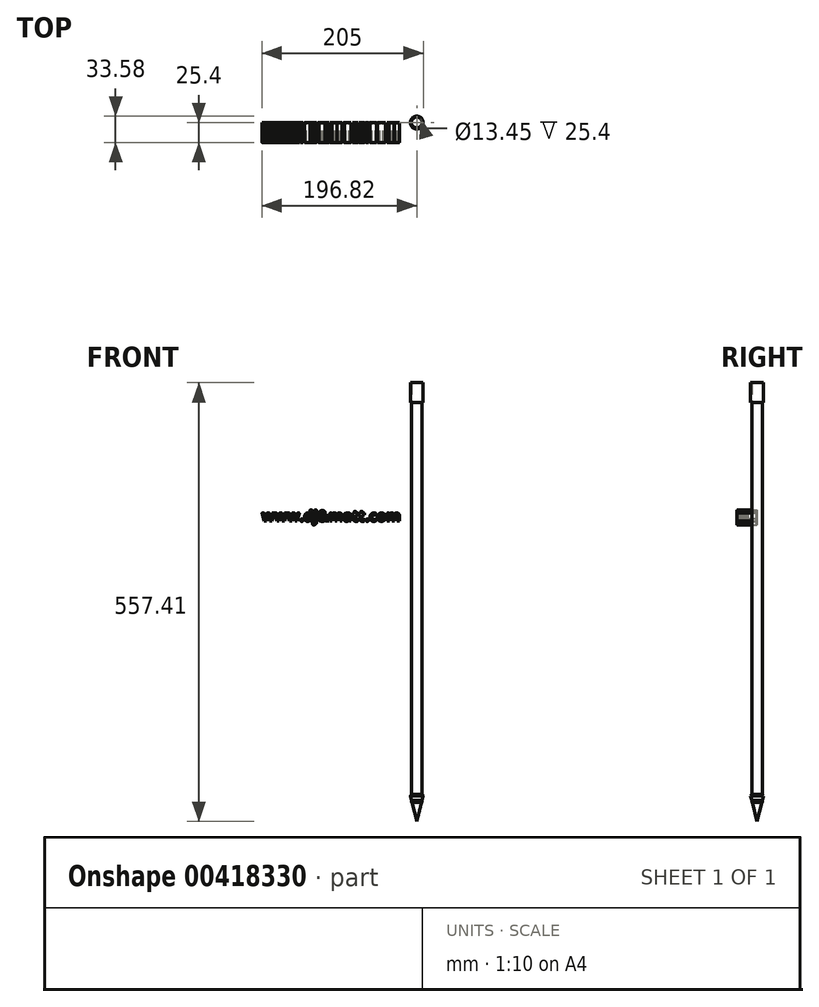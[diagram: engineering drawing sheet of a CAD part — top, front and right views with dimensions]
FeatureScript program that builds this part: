
annotation { "Feature Type Name" : "Feature", "Feature Type Description" : "" }
export const myFeature = defineFeature(function(context is Context, id is Id, definition is map)
    precondition{}
    {
        {
            var Q0;
            Q0=qCreatedBy(makeId("Top.planeOp"),FACE);
            var sketch = newSketch(context, id + "F0", { "sketchPlane" : qUnion([Q0])});
            skCircle(sketch, "E0", {"center": v(0, 0) * mm, "radius": 6.72 * mm});
            skSolve(sketch);
        }
        {
            var Q0;
            Q0=makeQuery(id+"F0.imprint","IMPRINT",FACE,{"disambiguationData":[TD([[makeQuery(id+"F0.imprint","IMPRINT",EDGE,{"derivedFrom":sQuery(id+"F0.wireOp",EDGE,"E0")}),1.0]])]});
            extrude(context, id + "F1", {"entities" : qUnion([Q0]), "depth" : 508 * mm});
        }
        {
            var Q0;
            Q0=qCreatedBy(makeId("Right.planeOp"),FACE);
            var sketch = newSketch(context, id + "F2", { "sketchPlane" : qUnion([Q0])});
            skLineSegment(sketch, "E1", {"start": v(0, -24.01) * mm, "end": v(8.18, 8.7) * mm});
            skLineSegment(sketch, "E2", {"start": v(8.18, 8.7) * mm, "end": v(0, 18.25) * mm});
            skLineSegment(sketch, "E3", {"start": v(0, 18.25) * mm, "end": v(0, -24.01) * mm});
            skSolve(sketch);
        }
        {
            var Q0;
            Q0=makeQuery(id+"F2.imprint","IMPRINT",FACE,{"disambiguationData":[TD([[makeQuery(id+"F2.imprint","IMPRINT",EDGE,{"derivedFrom":sQuery(id+"F2.wireOp",EDGE,"E1")}),1.0]])]});
            var Q1;
            Q1=sQuery(id+"F2.wireOp",EDGE,"E3");
            revolve(context, id + "F3", {"operationType" : NewBodyOperationType.ADD, "entities" : qUnion([Q0]), "axis" : qUnion([Q1]), "revolveType" : RevolveType.FULL});
        }
        {
            var Q0;
            Q0=makeQuery(id+"F1.opExtrude","CAP_FACE",FACE,{"disambiguationData":[OSD([sQuery(id+"F0.wireOp",EDGE,"E0")])],"isStart":false});
            var sketch = newSketch(context, id + "F4", { "sketchPlane" : qUnion([Q0])});
            skCircle(sketch, "E4", {"center": v(0, 0) * mm, "radius": 8.1 * mm});
            skSolve(sketch);
        }
        {
            var Q0;
            Q0=makeQuery(id+"F4.imprint","IMPRINT",FACE,{"disambiguationData":[TD([[makeQuery(id+"F4.imprint","IMPRINT",EDGE,{"derivedFrom":sQuery(id+"F4.wireOp",EDGE,"E4")}),1.0]])]});
            extrude(context, id + "F5", {"entities" : qUnion([Q0]), "depth" : 25.4 * mm});
        }
        {
            var Q0;
            Q0=qCreatedBy(makeId("Front.planeOp"),FACE);
            var sketch = newSketch(context, id + "F6", { "sketchPlane" : qUnion([Q0])});
            skText(sketch, "E5", { "text": "www.dj&matt.com", "fontName": "OpenSans-Bold.ttf"});
            const initialGuessF6  = {"E5": [-0.197, 0.35733, 1, 0, 0.01351]};
            skSetInitialGuess(sketch, initialGuessF6);
            skSolve(sketch);
        }
        {
            var Q0;
            Q0 = qSketchRegion(id + "F6", true);
            extrude(context, id + "F7", {"entities" : qUnion([Q0]), "depth" : 25.4 * mm});
        }
        {
            var Q0;
            Q0=makeQuery(id+"F7.opExtrude","CAP_EDGE",EDGE,{"disambiguationData":[OSD([sQuery(id+"F6.wireOp",EDGE,"E5.sketch_text.stroke-31")])],"isStart":false});
            var Q1;
            Q1=makeQuery(id+"F7.opExtrude","CAP_EDGE",EDGE,{"disambiguationData":[OSD([sQuery(id+"F6.wireOp",EDGE,"E5.sketch_text.stroke-50")])],"isStart":false});
            var Q2;
            Q2=makeQuery(id+"F7.opExtrude","CAP_EDGE",EDGE,{"disambiguationData":[OSD([sQuery(id+"F6.wireOp",EDGE,"E5.sketch_text.stroke-25")])],"isStart":false});
            var Q3;
            Q3=makeQuery(id+"F7.opExtrude","CAP_EDGE",EDGE,{"disambiguationData":[OSD([sQuery(id+"F6.wireOp",EDGE,"E5.sketch_text.stroke-5")])],"isStart":false});
            var Q4;
            Q4=makeQuery(id+"F7.opExtrude","CAP_EDGE",EDGE,{"disambiguationData":[OSD([sQuery(id+"F6.wireOp",EDGE,"E5.sketch_text.stroke-24")])],"isStart":false});
            var Q5;
            Q5=makeQuery(id+"F7.opExtrude","CAP_EDGE",EDGE,{"disambiguationData":[OSD([sQuery(id+"F6.wireOp",EDGE,"E5.sketch_text.stroke-76")])],"isStart":false});
            var Q6;
            Q6=makeQuery(id+"F7.opExtrude","CAP_EDGE",EDGE,{"disambiguationData":[OSD([sQuery(id+"F6.wireOp",EDGE,"E5.sketch_text.stroke-57")])],"isStart":false});
            var Q7;
            Q7=makeQuery(id+"F7.opExtrude","CAP_EDGE",EDGE,{"disambiguationData":[OSD([sQuery(id+"F6.wireOp",EDGE,"E5.sketch_text.stroke-51")])],"isStart":false});
            var Q8;
            Q8=makeQuery(id+"F7.opExtrude","CAP_EDGE",EDGE,{"disambiguationData":[OSD([sQuery(id+"F6.wireOp",EDGE,"E5.sketch_text.stroke-32")])],"isStart":false});
            var Q9;
            Q9=makeQuery(id+"F7.opExtrude","CAP_EDGE",EDGE,{"disambiguationData":[OSD([sQuery(id+"F6.wireOp",EDGE,"E5.sketch_text.stroke-30")])],"isStart":false});
            var Q10;
            Q10=makeQuery(id+"F7.opExtrude","CAP_EDGE",EDGE,{"disambiguationData":[OSD([sQuery(id+"F6.wireOp",EDGE,"E5.sketch_text.stroke-29")])],"isStart":false});
            var Q11;
            Q11=makeQuery(id+"F7.opExtrude","CAP_EDGE",EDGE,{"disambiguationData":[OSD([sQuery(id+"F6.wireOp",EDGE,"E5.sketch_text.stroke-27")])],"isStart":false});
            var Q12;
            Q12=makeQuery(id+"F7.opExtrude","CAP_EDGE",EDGE,{"disambiguationData":[OSD([sQuery(id+"F6.wireOp",EDGE,"E5.sketch_text.stroke-26")])],"isStart":false});
            var Q13;
            Q13=makeQuery(id+"F7.opExtrude","CAP_EDGE",EDGE,{"disambiguationData":[OSD([sQuery(id+"F6.wireOp",EDGE,"E5.sketch_text.stroke-49")])],"isStart":false});
            var Q14;
            Q14=makeQuery(id+"F7.opExtrude","CAP_EDGE",EDGE,{"disambiguationData":[OSD([sQuery(id+"F6.wireOp",EDGE,"E5.sketch_text.stroke-109")])],"isStart":false});
            var Q15;
            Q15=makeQuery(id+"F7.opExtrude","CAP_EDGE",EDGE,{"disambiguationData":[OSD([sQuery(id+"F6.wireOp",EDGE,"E5.sketch_text.stroke-117")])],"isStart":false});
            var Q16;
            Q16=makeQuery(id+"F7.opExtrude","CAP_EDGE",EDGE,{"disambiguationData":[OSD([sQuery(id+"F6.wireOp",EDGE,"E5.sketch_text.stroke-118")])],"isStart":false});
            var Q17;
            Q17=makeQuery(id+"F7.opExtrude","CAP_EDGE",EDGE,{"disambiguationData":[OSD([sQuery(id+"F6.wireOp",EDGE,"E5.sketch_text.stroke-97")])],"isStart":false});
            var Q18;
            Q18=makeQuery(id+"F7.opExtrude","CAP_EDGE",EDGE,{"disambiguationData":[OSD([sQuery(id+"F6.wireOp",EDGE,"E5.sketch_text.stroke-99")])],"isStart":false});
            var Q19;
            Q19=makeQuery(id+"F7.opExtrude","CAP_EDGE",EDGE,{"disambiguationData":[OSD([sQuery(id+"F6.wireOp",EDGE,"E5.sketch_text.stroke-86")])],"isStart":false});
            var Q20;
            Q20=makeQuery(id+"F7.opExtrude","CAP_EDGE",EDGE,{"disambiguationData":[OSD([sQuery(id+"F6.wireOp",EDGE,"E5.sketch_text.stroke-87")])],"isStart":false});
            var Q21;
            Q21=makeQuery(id+"F7.opExtrude","CAP_EDGE",EDGE,{"disambiguationData":[OSD([sQuery(id+"F6.wireOp",EDGE,"E5.sketch_text.stroke-96")])],"isStart":false});
            var Q22;
            Q22=makeQuery(id+"F7.opExtrude","CAP_EDGE",EDGE,{"disambiguationData":[OSD([sQuery(id+"F6.wireOp",EDGE,"E5.sketch_text.stroke-85")])],"isStart":false});
            var Q23;
            Q23=makeQuery(id+"F7.opExtrude","CAP_EDGE",EDGE,{"disambiguationData":[OSD([sQuery(id+"F6.wireOp",EDGE,"E5.sketch_text.stroke-84")])],"isStart":false});
            var Q24;
            Q24=makeQuery(id+"F7.opExtrude","CAP_EDGE",EDGE,{"disambiguationData":[OSD([sQuery(id+"F6.wireOp",EDGE,"E5.sketch_text.stroke-83")])],"isStart":false});
            var Q25;
            Q25=makeQuery(id+"F7.opExtrude","CAP_EDGE",EDGE,{"disambiguationData":[OSD([sQuery(id+"F6.wireOp",EDGE,"E5.sketch_text.stroke-82")])],"isStart":false});
            var Q26;
            Q26=makeQuery(id+"F7.opExtrude","CAP_EDGE",EDGE,{"disambiguationData":[OSD([sQuery(id+"F6.wireOp",EDGE,"E5.sketch_text.stroke-1")])],"isStart":false});
            var Q27;
            Q27=makeQuery(id+"F7.opExtrude","CAP_EDGE",EDGE,{"disambiguationData":[OSD([sQuery(id+"F6.wireOp",EDGE,"E5.sketch_text.stroke-18")])],"isStart":false});
            var Q28;
            Q28=makeQuery(id+"F7.opExtrude","CAP_EDGE",EDGE,{"disambiguationData":[OSD([sQuery(id+"F6.wireOp",EDGE,"E5.sketch_text.stroke-3")])],"isStart":false});
            var Q29;
            Q29=makeQuery(id+"F7.opExtrude","CAP_EDGE",EDGE,{"disambiguationData":[OSD([sQuery(id+"F6.wireOp",EDGE,"E5.sketch_text.stroke-4")])],"isStart":false});
            var Q30;
            Q30=makeQuery(id+"F7.opExtrude","CAP_EDGE",EDGE,{"disambiguationData":[OSD([sQuery(id+"F6.wireOp",EDGE,"E5.sketch_text.stroke-6")])],"isStart":false});
            var Q31;
            Q31=makeQuery(id+"F7.opExtrude","CAP_EDGE",EDGE,{"disambiguationData":[OSD([sQuery(id+"F6.wireOp",EDGE,"E5.sketch_text.stroke-22")])],"isStart":false});
            var Q32;
            Q32=makeQuery(id+"F7.opExtrude","CAP_EDGE",EDGE,{"disambiguationData":[OSD([sQuery(id+"F6.wireOp",EDGE,"E5.sketch_text.stroke-23")])],"isStart":false});
            var Q33;
            Q33=makeQuery(id+"F7.opExtrude","CAP_EDGE",EDGE,{"disambiguationData":[OSD([sQuery(id+"F6.wireOp",EDGE,"E5.sketch_text.stroke-0")])],"isStart":false});
            var Q34;
            Q34=makeQuery(id+"F7.opExtrude","CAP_EDGE",EDGE,{"disambiguationData":[OSD([sQuery(id+"F6.wireOp",EDGE,"E5.sketch_text.stroke-56")])],"isStart":false});
            var Q35;
            Q35=makeQuery(id+"F7.opExtrude","CAP_EDGE",EDGE,{"disambiguationData":[OSD([sQuery(id+"F6.wireOp",EDGE,"E5.sketch_text.stroke-55")])],"isStart":false});
            var Q36;
            Q36=makeQuery(id+"F7.opExtrude","CAP_EDGE",EDGE,{"disambiguationData":[OSD([sQuery(id+"F6.wireOp",EDGE,"E5.sketch_text.stroke-54")])],"isStart":false});
            var Q37;
            Q37=makeQuery(id+"F7.opExtrude","CAP_EDGE",EDGE,{"disambiguationData":[OSD([sQuery(id+"F6.wireOp",EDGE,"E5.sketch_text.stroke-77")])],"isStart":false});
            var Q38;
            Q38=makeQuery(id+"F7.opExtrude","CAP_EDGE",EDGE,{"disambiguationData":[OSD([sQuery(id+"F6.wireOp",EDGE,"E5.sketch_text.stroke-53")])],"isStart":false});
            var Q39;
            Q39=makeQuery(id+"F7.opExtrude","CAP_EDGE",EDGE,{"disambiguationData":[OSD([sQuery(id+"F6.wireOp",EDGE,"E5.sketch_text.stroke-52")])],"isStart":false});
            var Q40;
            Q40=makeQuery(id+"F7.opExtrude","CAP_EDGE",EDGE,{"disambiguationData":[OSD([sQuery(id+"F6.wireOp",EDGE,"E5.sketch_text.stroke-75")])],"isStart":false});
            var Q41;
            Q41=makeQuery(id+"F7.opExtrude","CAP_EDGE",EDGE,{"disambiguationData":[OSD([sQuery(id+"F6.wireOp",EDGE,"E5.sketch_text.stroke-74")])],"isStart":false});
            var Q42;
            Q42=makeQuery(id+"F7.opExtrude","CAP_EDGE",EDGE,{"disambiguationData":[OSD([sQuery(id+"F6.wireOp",EDGE,"E5.sketch_text.stroke-58")])],"isStart":false});
            var Q43;
            Q43=makeQuery(id+"F7.opExtrude","CAP_EDGE",EDGE,{"disambiguationData":[OSD([sQuery(id+"F6.wireOp",EDGE,"E5.sketch_text.stroke-124")])],"isStart":false});
            var Q44;
            Q44=makeQuery(id+"F7.opExtrude","CAP_EDGE",EDGE,{"disambiguationData":[OSD([sQuery(id+"F6.wireOp",EDGE,"E5.sketch_text.stroke-125")])],"isStart":false});
            var Q45;
            Q45=makeQuery(id+"F7.opExtrude","CAP_EDGE",EDGE,{"disambiguationData":[OSD([sQuery(id+"F6.wireOp",EDGE,"E5.sketch_text.stroke-126")])],"isStart":false});
            var Q46;
            Q46=makeQuery(id+"F7.opExtrude","CAP_EDGE",EDGE,{"disambiguationData":[OSD([sQuery(id+"F6.wireOp",EDGE,"E5.sketch_text.stroke-127")])],"isStart":false});
            var Q47;
            Q47=makeQuery(id+"F7.opExtrude","CAP_EDGE",EDGE,{"disambiguationData":[OSD([sQuery(id+"F6.wireOp",EDGE,"E5.sketch_text.stroke-128")])],"isStart":false});
            var Q48;
            Q48=makeQuery(id+"F7.opExtrude","CAP_EDGE",EDGE,{"disambiguationData":[OSD([sQuery(id+"F6.wireOp",EDGE,"E5.sketch_text.stroke-185")])],"isStart":false});
            var Q49;
            Q49=makeQuery(id+"F7.opExtrude","CAP_EDGE",EDGE,{"disambiguationData":[OSD([sQuery(id+"F6.wireOp",EDGE,"E5.sketch_text.stroke-162")])],"isStart":false});
            var Q50;
            Q50=makeQuery(id+"F7.opExtrude","CAP_EDGE",EDGE,{"disambiguationData":[OSD([sQuery(id+"F6.wireOp",EDGE,"E5.sketch_text.stroke-178")])],"isStart":false});
            var Q51;
            Q51=makeQuery(id+"F7.opExtrude","CAP_EDGE",EDGE,{"disambiguationData":[OSD([sQuery(id+"F6.wireOp",EDGE,"E5.sketch_text.stroke-179")])],"isStart":false});
            var Q52;
            Q52=makeQuery(id+"F7.opExtrude","CAP_EDGE",EDGE,{"disambiguationData":[OSD([sQuery(id+"F6.wireOp",EDGE,"E5.sketch_text.stroke-164")])],"isStart":false});
            var Q53;
            Q53=makeQuery(id+"F7.opExtrude","CAP_EDGE",EDGE,{"disambiguationData":[OSD([sQuery(id+"F6.wireOp",EDGE,"E5.sketch_text.stroke-165")])],"isStart":false});
            var Q54;
            Q54=makeQuery(id+"F7.opExtrude","CAP_EDGE",EDGE,{"disambiguationData":[OSD([sQuery(id+"F6.wireOp",EDGE,"E5.sketch_text.stroke-158")])],"isStart":false});
            var Q55;
            Q55=makeQuery(id+"F7.opExtrude","CAP_EDGE",EDGE,{"disambiguationData":[OSD([sQuery(id+"F6.wireOp",EDGE,"E5.sketch_text.stroke-183")])],"isStart":false});
            var Q56;
            Q56=makeQuery(id+"F7.opExtrude","CAP_EDGE",EDGE,{"disambiguationData":[OSD([sQuery(id+"F6.wireOp",EDGE,"E5.sketch_text.stroke-186")])],"isStart":false});
            var Q57;
            Q57=makeQuery(id+"F7.opExtrude","CAP_EDGE",EDGE,{"disambiguationData":[OSD([sQuery(id+"F6.wireOp",EDGE,"E5.sketch_text.stroke-202")])],"isStart":false});
            var Q58;
            Q58=makeQuery(id+"F7.opExtrude","CAP_EDGE",EDGE,{"disambiguationData":[OSD([sQuery(id+"F6.wireOp",EDGE,"E5.sketch_text.stroke-203")])],"isStart":false});
            var Q59;
            Q59=makeQuery(id+"F7.opExtrude","CAP_EDGE",EDGE,{"disambiguationData":[OSD([sQuery(id+"F6.wireOp",EDGE,"E5.sketch_text.stroke-188")])],"isStart":false});
            var Q60;
            Q60=makeQuery(id+"F7.opExtrude","CAP_EDGE",EDGE,{"disambiguationData":[OSD([sQuery(id+"F6.wireOp",EDGE,"E5.sketch_text.stroke-189")])],"isStart":false});
            var Q61;
            Q61=makeQuery(id+"F7.opExtrude","CAP_EDGE",EDGE,{"disambiguationData":[OSD([sQuery(id+"F6.wireOp",EDGE,"E5.sketch_text.stroke-190")])],"isStart":false});
            var Q62;
            Q62=makeQuery(id+"F7.opExtrude","CAP_EDGE",EDGE,{"disambiguationData":[OSD([sQuery(id+"F6.wireOp",EDGE,"E5.sketch_text.stroke-191")])],"isStart":false});
            var Q63;
            Q63=makeQuery(id+"F7.opExtrude","CAP_EDGE",EDGE,{"disambiguationData":[OSD([sQuery(id+"F6.wireOp",EDGE,"E5.sketch_text.stroke-217")])],"isStart":false});
            var Q64;
            Q64=makeQuery(id+"F7.opExtrude","CAP_EDGE",EDGE,{"disambiguationData":[OSD([sQuery(id+"F6.wireOp",EDGE,"E5.sketch_text.stroke-213")])],"isStart":false});
            var Q65;
            Q65=makeQuery(id+"F7.opExtrude","CAP_EDGE",EDGE,{"disambiguationData":[OSD([sQuery(id+"F6.wireOp",EDGE,"E5.sketch_text.stroke-214")])],"isStart":false});
            var Q66;
            Q66=makeQuery(id+"F7.opExtrude","CAP_EDGE",EDGE,{"disambiguationData":[OSD([sQuery(id+"F6.wireOp",EDGE,"E5.sketch_text.stroke-215")])],"isStart":false});
            var Q67;
            Q67=makeQuery(id+"F7.opExtrude","CAP_EDGE",EDGE,{"disambiguationData":[OSD([sQuery(id+"F6.wireOp",EDGE,"E5.sketch_text.stroke-233")])],"isStart":false});
            var Q68;
            Q68=makeQuery(id+"F7.opExtrude","CAP_EDGE",EDGE,{"disambiguationData":[OSD([sQuery(id+"F6.wireOp",EDGE,"E5.sketch_text.stroke-230")])],"isStart":false});
            var Q69;
            Q69=makeQuery(id+"F7.opExtrude","CAP_EDGE",EDGE,{"disambiguationData":[OSD([sQuery(id+"F6.wireOp",EDGE,"E5.sketch_text.stroke-231")])],"isStart":false});
            var Q70;
            Q70=makeQuery(id+"F7.opExtrude","CAP_EDGE",EDGE,{"disambiguationData":[OSD([sQuery(id+"F6.wireOp",EDGE,"E5.sketch_text.stroke-232")])],"isStart":false});
            var Q71;
            Q71=makeQuery(id+"F7.opExtrude","CAP_EDGE",EDGE,{"disambiguationData":[OSD([sQuery(id+"F6.wireOp",EDGE,"E5.sketch_text.stroke-251")])],"isStart":false});
            var Q72;
            Q72=makeQuery(id+"F7.opExtrude","CAP_EDGE",EDGE,{"disambiguationData":[OSD([sQuery(id+"F6.wireOp",EDGE,"E5.sketch_text.stroke-252")])],"isStart":false});
            var Q73;
            Q73=makeQuery(id+"F7.opExtrude","CAP_EDGE",EDGE,{"disambiguationData":[OSD([sQuery(id+"F6.wireOp",EDGE,"E5.sketch_text.stroke-253")])],"isStart":false});
            var Q74;
            Q74=makeQuery(id+"F7.opExtrude","CAP_EDGE",EDGE,{"disambiguationData":[OSD([sQuery(id+"F6.wireOp",EDGE,"E5.sketch_text.stroke-254")])],"isStart":false});
            var Q75;
            Q75=makeQuery(id+"F7.opExtrude","CAP_EDGE",EDGE,{"disambiguationData":[OSD([sQuery(id+"F6.wireOp",EDGE,"E5.sketch_text.stroke-267")])],"isStart":false});
            var Q76;
            Q76=makeQuery(id+"F7.opExtrude","CAP_EDGE",EDGE,{"disambiguationData":[OSD([sQuery(id+"F6.wireOp",EDGE,"E5.sketch_text.stroke-268")])],"isStart":false});
            var Q77;
            Q77=makeQuery(id+"F7.opExtrude","CAP_EDGE",EDGE,{"disambiguationData":[OSD([sQuery(id+"F6.wireOp",EDGE,"E5.sketch_text.stroke-255")])],"isStart":false});
            var Q78;
            Q78=makeQuery(id+"F7.opExtrude","CAP_EDGE",EDGE,{"disambiguationData":[OSD([sQuery(id+"F6.wireOp",EDGE,"E5.sketch_text.stroke-281")])],"isStart":false});
            var Q79;
            Q79=makeQuery(id+"F7.opExtrude","CAP_EDGE",EDGE,{"disambiguationData":[OSD([sQuery(id+"F6.wireOp",EDGE,"E5.sketch_text.stroke-277")])],"isStart":false});
            var Q80;
            Q80=makeQuery(id+"F7.opExtrude","CAP_EDGE",EDGE,{"disambiguationData":[OSD([sQuery(id+"F6.wireOp",EDGE,"E5.sketch_text.stroke-278")])],"isStart":false});
            var Q81;
            Q81=makeQuery(id+"F7.opExtrude","CAP_EDGE",EDGE,{"disambiguationData":[OSD([sQuery(id+"F6.wireOp",EDGE,"E5.sketch_text.stroke-279")])],"isStart":false});
            var Q82;
            Q82=makeQuery(id+"F7.opExtrude","CAP_EDGE",EDGE,{"disambiguationData":[OSD([sQuery(id+"F6.wireOp",EDGE,"E5.sketch_text.stroke-280")])],"isStart":false});
            var Q83;
            Q83=makeQuery(id+"F7.opExtrude","CAP_EDGE",EDGE,{"disambiguationData":[OSD([sQuery(id+"F6.wireOp",EDGE,"E5.sketch_text.stroke-290")])],"isStart":false});
            var Q84;
            Q84=makeQuery(id+"F7.opExtrude","CAP_EDGE",EDGE,{"disambiguationData":[OSD([sQuery(id+"F6.wireOp",EDGE,"E5.sketch_text.stroke-314")])],"isStart":false});
            var Q85;
            Q85=makeQuery(id+"F7.opExtrude","CAP_EDGE",EDGE,{"disambiguationData":[OSD([sQuery(id+"F6.wireOp",EDGE,"E5.sketch_text.stroke-307")])],"isStart":false});
            var Q86;
            Q86=makeQuery(id+"F7.opExtrude","CAP_EDGE",EDGE,{"disambiguationData":[OSD([sQuery(id+"F6.wireOp",EDGE,"E5.sketch_text.stroke-308")])],"isStart":false});
            var Q87;
            Q87=makeQuery(id+"F7.opExtrude","CAP_EDGE",EDGE,{"disambiguationData":[OSD([sQuery(id+"F6.wireOp",EDGE,"E5.sketch_text.stroke-293")])],"isStart":false});
            var Q88;
            Q88=makeQuery(id+"F7.opExtrude","CAP_EDGE",EDGE,{"disambiguationData":[OSD([sQuery(id+"F6.wireOp",EDGE,"E5.sketch_text.stroke-294")])],"isStart":false});
            var Q89;
            Q89=makeQuery(id+"F7.opExtrude","CAP_EDGE",EDGE,{"disambiguationData":[OSD([sQuery(id+"F6.wireOp",EDGE,"E5.sketch_text.stroke-287")])],"isStart":false});
            var Q90;
            Q90=makeQuery(id+"F7.opExtrude","CAP_EDGE",EDGE,{"disambiguationData":[OSD([sQuery(id+"F6.wireOp",EDGE,"E5.sketch_text.stroke-311")])],"isStart":false});
            var Q91;
            Q91=makeQuery(id+"F7.opExtrude","CAP_EDGE",EDGE,{"disambiguationData":[OSD([sQuery(id+"F6.wireOp",EDGE,"E5.sketch_text.stroke-48")])],"isStart":false});
            var Q92;
            Q92=makeQuery(id+"F7.opExtrude","CAP_EDGE",EDGE,{"disambiguationData":[OSD([sQuery(id+"F6.wireOp",EDGE,"E5.sketch_text.stroke-45")])],"isStart":false});
            var Q93;
            Q93=makeQuery(id+"F7.opExtrude","CAP_EDGE",EDGE,{"disambiguationData":[OSD([sQuery(id+"F6.wireOp",EDGE,"E5.sketch_text.stroke-44")])],"isStart":false});
            var Q94;
            Q94=makeQuery(id+"F7.opExtrude","CAP_EDGE",EDGE,{"disambiguationData":[OSD([sQuery(id+"F6.wireOp",EDGE,"E5.sketch_text.stroke-36")])],"isStart":false});
            var Q95;
            Q95=makeQuery(id+"F7.opExtrude","CAP_EDGE",EDGE,{"disambiguationData":[OSD([sQuery(id+"F6.wireOp",EDGE,"E5.sketch_text.stroke-28")])],"isStart":false});
            var Q96;
            Q96=makeQuery(id+"F7.opExtrude","CAP_EDGE",EDGE,{"disambiguationData":[OSD([sQuery(id+"F6.wireOp",EDGE,"E5.sketch_text.stroke-34")])],"isStart":false});
            var Q97;
            Q97=makeQuery(id+"F7.opExtrude","CAP_EDGE",EDGE,{"disambiguationData":[OSD([sQuery(id+"F6.wireOp",EDGE,"E5.sketch_text.stroke-33")])],"isStart":false});
            var Q98;
            Q98=makeQuery(id+"F7.opExtrude","CAP_EDGE",EDGE,{"disambiguationData":[OSD([sQuery(id+"F6.wireOp",EDGE,"E5.sketch_text.stroke-115")])],"isStart":false});
            var Q99;
            Q99=makeQuery(id+"F7.opExtrude","CAP_EDGE",EDGE,{"disambiguationData":[OSD([sQuery(id+"F6.wireOp",EDGE,"E5.sketch_text.stroke-116")])],"isStart":false});
            var Q100;
            Q100=makeQuery(id+"F7.opExtrude","CAP_EDGE",EDGE,{"disambiguationData":[OSD([sQuery(id+"F6.wireOp",EDGE,"E5.sketch_text.stroke-110")])],"isStart":false});
            var Q101;
            Q101=makeQuery(id+"F7.opExtrude","CAP_EDGE",EDGE,{"disambiguationData":[OSD([sQuery(id+"F6.wireOp",EDGE,"E5.sketch_text.stroke-111")])],"isStart":false});
            var Q102;
            Q102=makeQuery(id+"F7.opExtrude","CAP_EDGE",EDGE,{"disambiguationData":[OSD([sQuery(id+"F6.wireOp",EDGE,"E5.sketch_text.stroke-112")])],"isStart":false});
            var Q103;
            Q103=makeQuery(id+"F7.opExtrude","CAP_EDGE",EDGE,{"disambiguationData":[OSD([sQuery(id+"F6.wireOp",EDGE,"E5.sketch_text.stroke-98")])],"isStart":false});
            var Q104;
            Q104=makeQuery(id+"F7.opExtrude","CAP_EDGE",EDGE,{"disambiguationData":[OSD([sQuery(id+"F6.wireOp",EDGE,"E5.sketch_text.stroke-100")])],"isStart":false});
            var Q105;
            Q105=makeQuery(id+"F7.opExtrude","CAP_EDGE",EDGE,{"disambiguationData":[OSD([sQuery(id+"F6.wireOp",EDGE,"E5.sketch_text.stroke-108")])],"isStart":false});
            var Q106;
            Q106=makeQuery(id+"F7.opExtrude","CAP_EDGE",EDGE,{"disambiguationData":[OSD([sQuery(id+"F6.wireOp",EDGE,"E5.sketch_text.stroke-88")])],"isStart":false});
            var Q107;
            Q107=makeQuery(id+"F7.opExtrude","CAP_EDGE",EDGE,{"disambiguationData":[OSD([sQuery(id+"F6.wireOp",EDGE,"E5.sketch_text.stroke-81")])],"isStart":false});
            var Q108;
            Q108=makeQuery(id+"F7.opExtrude","CAP_EDGE",EDGE,{"disambiguationData":[OSD([sQuery(id+"F6.wireOp",EDGE,"E5.sketch_text.stroke-78")])],"isStart":false});
            var Q109;
            Q109=makeQuery(id+"F7.opExtrude","CAP_EDGE",EDGE,{"disambiguationData":[OSD([sQuery(id+"F6.wireOp",EDGE,"E5.sketch_text.stroke-9")])],"isStart":false});
            var Q110;
            Q110=makeQuery(id+"F7.opExtrude","CAP_EDGE",EDGE,{"disambiguationData":[OSD([sQuery(id+"F6.wireOp",EDGE,"E5.sketch_text.stroke-2")])],"isStart":false});
            var Q111;
            Q111=makeQuery(id+"F7.opExtrude","CAP_EDGE",EDGE,{"disambiguationData":[OSD([sQuery(id+"F6.wireOp",EDGE,"E5.sketch_text.stroke-19")])],"isStart":false});
            var Q112;
            Q112=makeQuery(id+"F7.opExtrude","CAP_EDGE",EDGE,{"disambiguationData":[OSD([sQuery(id+"F6.wireOp",EDGE,"E5.sketch_text.stroke-7")])],"isStart":false});
            var Q113;
            Q113=makeQuery(id+"F7.opExtrude","CAP_EDGE",EDGE,{"disambiguationData":[OSD([sQuery(id+"F6.wireOp",EDGE,"E5.sketch_text.stroke-70")])],"isStart":false});
            var Q114;
            Q114=makeQuery(id+"F7.opExtrude","CAP_EDGE",EDGE,{"disambiguationData":[OSD([sQuery(id+"F6.wireOp",EDGE,"E5.sketch_text.stroke-60")])],"isStart":false});
            var Q115;
            Q115=makeQuery(id+"F7.opExtrude","CAP_EDGE",EDGE,{"disambiguationData":[OSD([sQuery(id+"F6.wireOp",EDGE,"E5.sketch_text.stroke-59")])],"isStart":false});
            var Q116;
            Q116=makeQuery(id+"F7.opExtrude","CAP_EDGE",EDGE,{"disambiguationData":[OSD([sQuery(id+"F6.wireOp",EDGE,"E5.sketch_text.stroke-129")])],"isStart":false});
            var Q117;
            Q117=makeQuery(id+"F7.opExtrude","CAP_EDGE",EDGE,{"disambiguationData":[OSD([sQuery(id+"F6.wireOp",EDGE,"E5.sketch_text.stroke-145")])],"isStart":false});
            var Q118;
            Q118=makeQuery(id+"F7.opExtrude","CAP_EDGE",EDGE,{"disambiguationData":[OSD([sQuery(id+"F6.wireOp",EDGE,"E5.sketch_text.stroke-146")])],"isStart":false});
            var Q119;
            Q119=makeQuery(id+"F7.opExtrude","CAP_EDGE",EDGE,{"disambiguationData":[OSD([sQuery(id+"F6.wireOp",EDGE,"E5.sketch_text.stroke-139")])],"isStart":false});
            var Q120;
            Q120=makeQuery(id+"F7.opExtrude","CAP_EDGE",EDGE,{"disambiguationData":[OSD([sQuery(id+"F6.wireOp",EDGE,"E5.sketch_text.stroke-147")])],"isStart":false});
            var Q121;
            Q121=makeQuery(id+"F7.opExtrude","CAP_EDGE",EDGE,{"disambiguationData":[OSD([sQuery(id+"F6.wireOp",EDGE,"E5.sketch_text.stroke-140")])],"isStart":false});
            var Q122;
            Q122=makeQuery(id+"F7.opExtrude","CAP_EDGE",EDGE,{"disambiguationData":[OSD([sQuery(id+"F6.wireOp",EDGE,"E5.sketch_text.stroke-143")])],"isStart":false});
            var Q123;
            Q123=makeQuery(id+"F7.opExtrude","CAP_EDGE",EDGE,{"disambiguationData":[OSD([sQuery(id+"F6.wireOp",EDGE,"E5.sketch_text.stroke-144")])],"isStart":false});
            var Q124;
            Q124=makeQuery(id+"F7.opExtrude","CAP_EDGE",EDGE,{"disambiguationData":[OSD([sQuery(id+"F6.wireOp",EDGE,"E5.sketch_text.stroke-169")])],"isStart":false});
            var Q125;
            Q125=makeQuery(id+"F7.opExtrude","CAP_EDGE",EDGE,{"disambiguationData":[OSD([sQuery(id+"F6.wireOp",EDGE,"E5.sketch_text.stroke-177")])],"isStart":false});
            var Q126;
            Q126=makeQuery(id+"F7.opExtrude","CAP_EDGE",EDGE,{"disambiguationData":[OSD([sQuery(id+"F6.wireOp",EDGE,"E5.sketch_text.stroke-163")])],"isStart":false});
            var Q127;
            Q127=makeQuery(id+"F7.opExtrude","CAP_EDGE",EDGE,{"disambiguationData":[OSD([sQuery(id+"F6.wireOp",EDGE,"E5.sketch_text.stroke-172")])],"isStart":false});
            var Q128;
            Q128=makeQuery(id+"F7.opExtrude","CAP_EDGE",EDGE,{"disambiguationData":[OSD([sQuery(id+"F6.wireOp",EDGE,"E5.sketch_text.stroke-180")])],"isStart":false});
            var Q129;
            Q129=makeQuery(id+"F7.opExtrude","CAP_EDGE",EDGE,{"disambiguationData":[OSD([sQuery(id+"F6.wireOp",EDGE,"E5.sketch_text.stroke-181")])],"isStart":false});
            var Q130;
            Q130=makeQuery(id+"F7.opExtrude","CAP_EDGE",EDGE,{"disambiguationData":[OSD([sQuery(id+"F6.wireOp",EDGE,"E5.sketch_text.stroke-166")])],"isStart":false});
            var Q131;
            Q131=makeQuery(id+"F7.opExtrude","CAP_EDGE",EDGE,{"disambiguationData":[OSD([sQuery(id+"F6.wireOp",EDGE,"E5.sketch_text.stroke-159")])],"isStart":false});
            var Q132;
            Q132=makeQuery(id+"F7.opExtrude","CAP_EDGE",EDGE,{"disambiguationData":[OSD([sQuery(id+"F6.wireOp",EDGE,"E5.sketch_text.stroke-160")])],"isStart":false});
            var Q133;
            Q133=makeQuery(id+"F7.opExtrude","CAP_EDGE",EDGE,{"disambiguationData":[OSD([sQuery(id+"F6.wireOp",EDGE,"E5.sketch_text.stroke-184")])],"isStart":false});
            var Q134;
            Q134=makeQuery(id+"F7.opExtrude","CAP_EDGE",EDGE,{"disambiguationData":[OSD([sQuery(id+"F6.wireOp",EDGE,"E5.sketch_text.stroke-193")])],"isStart":false});
            var Q135;
            Q135=makeQuery(id+"F7.opExtrude","CAP_EDGE",EDGE,{"disambiguationData":[OSD([sQuery(id+"F6.wireOp",EDGE,"E5.sketch_text.stroke-201")])],"isStart":false});
            var Q136;
            Q136=makeQuery(id+"F7.opExtrude","CAP_EDGE",EDGE,{"disambiguationData":[OSD([sQuery(id+"F6.wireOp",EDGE,"E5.sketch_text.stroke-187")])],"isStart":false});
            var Q137;
            Q137=makeQuery(id+"F7.opExtrude","CAP_EDGE",EDGE,{"disambiguationData":[OSD([sQuery(id+"F6.wireOp",EDGE,"E5.sketch_text.stroke-207")])],"isStart":false});
            var Q138;
            Q138=makeQuery(id+"F7.opExtrude","CAP_EDGE",EDGE,{"disambiguationData":[OSD([sQuery(id+"F6.wireOp",EDGE,"E5.sketch_text.stroke-192")])],"isStart":false});
            var Q139;
            Q139=makeQuery(id+"F7.opExtrude","CAP_EDGE",EDGE,{"disambiguationData":[OSD([sQuery(id+"F6.wireOp",EDGE,"E5.sketch_text.stroke-208")])],"isStart":false});
            var Q140;
            Q140=makeQuery(id+"F7.opExtrude","CAP_EDGE",EDGE,{"disambiguationData":[OSD([sQuery(id+"F6.wireOp",EDGE,"E5.sketch_text.stroke-218")])],"isStart":false});
            var Q141;
            Q141=makeQuery(id+"F7.opExtrude","CAP_EDGE",EDGE,{"disambiguationData":[OSD([sQuery(id+"F6.wireOp",EDGE,"E5.sketch_text.stroke-211")])],"isStart":false});
            var Q142;
            Q142=makeQuery(id+"F7.opExtrude","CAP_EDGE",EDGE,{"disambiguationData":[OSD([sQuery(id+"F6.wireOp",EDGE,"E5.sketch_text.stroke-219")])],"isStart":false});
            var Q143;
            Q143=makeQuery(id+"F7.opExtrude","CAP_EDGE",EDGE,{"disambiguationData":[OSD([sQuery(id+"F6.wireOp",EDGE,"E5.sketch_text.stroke-227")])],"isStart":false});
            var Q144;
            Q144=makeQuery(id+"F7.opExtrude","CAP_EDGE",EDGE,{"disambiguationData":[OSD([sQuery(id+"F6.wireOp",EDGE,"E5.sketch_text.stroke-212")])],"isStart":false});
            var Q145;
            Q145=makeQuery(id+"F7.opExtrude","CAP_EDGE",EDGE,{"disambiguationData":[OSD([sQuery(id+"F6.wireOp",EDGE,"E5.sketch_text.stroke-228")])],"isStart":false});
            var Q146;
            Q146=makeQuery(id+"F7.opExtrude","CAP_EDGE",EDGE,{"disambiguationData":[OSD([sQuery(id+"F6.wireOp",EDGE,"E5.sketch_text.stroke-216")])],"isStart":false});
            var Q147;
            Q147=makeQuery(id+"F7.opExtrude","CAP_EDGE",EDGE,{"disambiguationData":[OSD([sQuery(id+"F6.wireOp",EDGE,"E5.sketch_text.stroke-234")])],"isStart":false});
            var Q148;
            Q148=makeQuery(id+"F7.opExtrude","CAP_EDGE",EDGE,{"disambiguationData":[OSD([sQuery(id+"F6.wireOp",EDGE,"E5.sketch_text.stroke-235")])],"isStart":false});
            var Q149;
            Q149=makeQuery(id+"F7.opExtrude","CAP_EDGE",EDGE,{"disambiguationData":[OSD([sQuery(id+"F6.wireOp",EDGE,"E5.sketch_text.stroke-229")])],"isStart":false});
            var Q150;
            Q150=makeQuery(id+"F7.opExtrude","CAP_EDGE",EDGE,{"disambiguationData":[OSD([sQuery(id+"F6.wireOp",EDGE,"E5.sketch_text.stroke-246")])],"isStart":false});
            var Q151;
            Q151=makeQuery(id+"F7.opExtrude","CAP_EDGE",EDGE,{"disambiguationData":[OSD([sQuery(id+"F6.wireOp",EDGE,"E5.sketch_text.stroke-250")])],"isStart":false});
            var Q152;
            Q152=makeQuery(id+"F7.opExtrude","CAP_EDGE",EDGE,{"disambiguationData":[OSD([sQuery(id+"F6.wireOp",EDGE,"E5.sketch_text.stroke-247")])],"isStart":false});
            var Q153;
            Q153=makeQuery(id+"F7.opExtrude","CAP_EDGE",EDGE,{"disambiguationData":[OSD([sQuery(id+"F6.wireOp",EDGE,"E5.sketch_text.stroke-265")])],"isStart":false});
            var Q154;
            Q154=makeQuery(id+"F7.opExtrude","CAP_EDGE",EDGE,{"disambiguationData":[OSD([sQuery(id+"F6.wireOp",EDGE,"E5.sketch_text.stroke-257")])],"isStart":false});
            var Q155;
            Q155=makeQuery(id+"F7.opExtrude","CAP_EDGE",EDGE,{"disambiguationData":[OSD([sQuery(id+"F6.wireOp",EDGE,"E5.sketch_text.stroke-266")])],"isStart":false});
            var Q156;
            Q156=makeQuery(id+"F7.opExtrude","CAP_EDGE",EDGE,{"disambiguationData":[OSD([sQuery(id+"F6.wireOp",EDGE,"E5.sketch_text.stroke-263")])],"isStart":false});
            var Q157;
            Q157=makeQuery(id+"F7.opExtrude","CAP_EDGE",EDGE,{"disambiguationData":[OSD([sQuery(id+"F6.wireOp",EDGE,"E5.sketch_text.stroke-264")])],"isStart":false});
            var Q158;
            Q158=makeQuery(id+"F7.opExtrude","CAP_EDGE",EDGE,{"disambiguationData":[OSD([sQuery(id+"F6.wireOp",EDGE,"E5.sketch_text.stroke-256")])],"isStart":false});
            var Q159;
            Q159=makeQuery(id+"F7.opExtrude","CAP_EDGE",EDGE,{"disambiguationData":[OSD([sQuery(id+"F6.wireOp",EDGE,"E5.sketch_text.stroke-282")])],"isStart":false});
            var Q160;
            Q160=makeQuery(id+"F7.opExtrude","CAP_EDGE",EDGE,{"disambiguationData":[OSD([sQuery(id+"F6.wireOp",EDGE,"E5.sketch_text.stroke-269")])],"isStart":false});
            var Q161;
            Q161=makeQuery(id+"F7.opExtrude","CAP_EDGE",EDGE,{"disambiguationData":[OSD([sQuery(id+"F6.wireOp",EDGE,"E5.sketch_text.stroke-285")])],"isStart":false});
            var Q162;
            Q162=makeQuery(id+"F7.opExtrude","CAP_EDGE",EDGE,{"disambiguationData":[OSD([sQuery(id+"F6.wireOp",EDGE,"E5.sketch_text.stroke-270")])],"isStart":false});
            var Q163;
            Q163=makeQuery(id+"F7.opExtrude","CAP_EDGE",EDGE,{"disambiguationData":[OSD([sQuery(id+"F6.wireOp",EDGE,"E5.sketch_text.stroke-286")])],"isStart":false});
            var Q164;
            Q164=makeQuery(id+"F7.opExtrude","CAP_EDGE",EDGE,{"disambiguationData":[OSD([sQuery(id+"F6.wireOp",EDGE,"E5.sketch_text.stroke-271")])],"isStart":false});
            var Q165;
            Q165=makeQuery(id+"F7.opExtrude","CAP_EDGE",EDGE,{"disambiguationData":[OSD([sQuery(id+"F6.wireOp",EDGE,"E5.sketch_text.stroke-272")])],"isStart":false});
            var Q166;
            Q166=makeQuery(id+"F7.opExtrude","CAP_EDGE",EDGE,{"disambiguationData":[OSD([sQuery(id+"F6.wireOp",EDGE,"E5.sketch_text.stroke-313")])],"isStart":false});
            var Q167;
            Q167=makeQuery(id+"F7.opExtrude","CAP_EDGE",EDGE,{"disambiguationData":[OSD([sQuery(id+"F6.wireOp",EDGE,"E5.sketch_text.stroke-306")])],"isStart":false});
            var Q168;
            Q168=makeQuery(id+"F7.opExtrude","CAP_EDGE",EDGE,{"disambiguationData":[OSD([sQuery(id+"F6.wireOp",EDGE,"E5.sketch_text.stroke-291")])],"isStart":false});
            var Q169;
            Q169=makeQuery(id+"F7.opExtrude","CAP_EDGE",EDGE,{"disambiguationData":[OSD([sQuery(id+"F6.wireOp",EDGE,"E5.sketch_text.stroke-292")])],"isStart":false});
            var Q170;
            Q170=makeQuery(id+"F7.opExtrude","CAP_EDGE",EDGE,{"disambiguationData":[OSD([sQuery(id+"F6.wireOp",EDGE,"E5.sketch_text.stroke-300")])],"isStart":false});
            var Q171;
            Q171=makeQuery(id+"F7.opExtrude","CAP_EDGE",EDGE,{"disambiguationData":[OSD([sQuery(id+"F6.wireOp",EDGE,"E5.sketch_text.stroke-301")])],"isStart":false});
            var Q172;
            Q172=makeQuery(id+"F7.opExtrude","CAP_EDGE",EDGE,{"disambiguationData":[OSD([sQuery(id+"F6.wireOp",EDGE,"E5.sketch_text.stroke-309")])],"isStart":false});
            var Q173;
            Q173=makeQuery(id+"F7.opExtrude","CAP_EDGE",EDGE,{"disambiguationData":[OSD([sQuery(id+"F6.wireOp",EDGE,"E5.sketch_text.stroke-295")])],"isStart":false});
            var Q174;
            Q174=makeQuery(id+"F7.opExtrude","CAP_EDGE",EDGE,{"disambiguationData":[OSD([sQuery(id+"F6.wireOp",EDGE,"E5.sketch_text.stroke-288")])],"isStart":false});
            var Q175;
            Q175=makeQuery(id+"F7.opExtrude","CAP_EDGE",EDGE,{"disambiguationData":[OSD([sQuery(id+"F6.wireOp",EDGE,"E5.sketch_text.stroke-296")])],"isStart":false});
            var Q176;
            Q176=makeQuery(id+"F7.opExtrude","CAP_EDGE",EDGE,{"disambiguationData":[OSD([sQuery(id+"F6.wireOp",EDGE,"E5.sketch_text.stroke-304")])],"isStart":false});
            var Q177;
            Q177=makeQuery(id+"F7.opExtrude","CAP_EDGE",EDGE,{"disambiguationData":[OSD([sQuery(id+"F6.wireOp",EDGE,"E5.sketch_text.stroke-312")])],"isStart":false});
            var Q178;
            Q178=makeQuery(id+"F7.opExtrude","CAP_EDGE",EDGE,{"disambiguationData":[OSD([sQuery(id+"F6.wireOp",EDGE,"E5.sketch_text.stroke-43")])],"isStart":false});
            var Q179;
            Q179=makeQuery(id+"F7.opExtrude","CAP_EDGE",EDGE,{"disambiguationData":[OSD([sQuery(id+"F6.wireOp",EDGE,"E5.sketch_text.stroke-39")])],"isStart":false});
            var Q180;
            Q180=makeQuery(id+"F7.opExtrude","CAP_EDGE",EDGE,{"disambiguationData":[OSD([sQuery(id+"F6.wireOp",EDGE,"E5.sketch_text.stroke-46")])],"isStart":false});
            var Q181;
            Q181=makeQuery(id+"F7.opExtrude","CAP_EDGE",EDGE,{"disambiguationData":[OSD([sQuery(id+"F6.wireOp",EDGE,"E5.sketch_text.stroke-38")])],"isStart":false});
            var Q182;
            Q182=makeQuery(id+"F7.opExtrude","CAP_EDGE",EDGE,{"disambiguationData":[OSD([sQuery(id+"F6.wireOp",EDGE,"E5.sketch_text.stroke-37")])],"isStart":false});
            var Q183;
            Q183=makeQuery(id+"F7.opExtrude","CAP_EDGE",EDGE,{"disambiguationData":[OSD([sQuery(id+"F6.wireOp",EDGE,"E5.sketch_text.stroke-35")])],"isStart":false});
            var Q184;
            Q184=makeQuery(id+"F7.opExtrude","CAP_EDGE",EDGE,{"disambiguationData":[OSD([sQuery(id+"F6.wireOp",EDGE,"E5.sketch_text.stroke-113")])],"isStart":false});
            var Q185;
            Q185=makeQuery(id+"F7.opExtrude","CAP_EDGE",EDGE,{"disambiguationData":[OSD([sQuery(id+"F6.wireOp",EDGE,"E5.sketch_text.stroke-89")])],"isStart":false});
            var Q186;
            Q186=makeQuery(id+"F7.opExtrude","CAP_EDGE",EDGE,{"disambiguationData":[OSD([sQuery(id+"F6.wireOp",EDGE,"E5.sketch_text.stroke-105")])],"isStart":false});
            var Q187;
            Q187=makeQuery(id+"F7.opExtrude","CAP_EDGE",EDGE,{"disambiguationData":[OSD([sQuery(id+"F6.wireOp",EDGE,"E5.sketch_text.stroke-107")])],"isStart":false});
            var Q188;
            Q188=makeQuery(id+"F7.opExtrude","CAP_EDGE",EDGE,{"disambiguationData":[OSD([sQuery(id+"F6.wireOp",EDGE,"E5.sketch_text.stroke-101")])],"isStart":false});
            var Q189;
            Q189=makeQuery(id+"F7.opExtrude","CAP_EDGE",EDGE,{"disambiguationData":[OSD([sQuery(id+"F6.wireOp",EDGE,"E5.sketch_text.stroke-94")])],"isStart":false});
            var Q190;
            Q190=makeQuery(id+"F7.opExtrude","CAP_EDGE",EDGE,{"disambiguationData":[OSD([sQuery(id+"F6.wireOp",EDGE,"E5.sketch_text.stroke-95")])],"isStart":false});
            var Q191;
            Q191=makeQuery(id+"F7.opExtrude","CAP_EDGE",EDGE,{"disambiguationData":[OSD([sQuery(id+"F6.wireOp",EDGE,"E5.sketch_text.stroke-104")])],"isStart":false});
            var Q192;
            Q192=makeQuery(id+"F7.opExtrude","CAP_EDGE",EDGE,{"disambiguationData":[OSD([sQuery(id+"F6.wireOp",EDGE,"E5.sketch_text.stroke-79")])],"isStart":false});
            var Q193;
            Q193=makeQuery(id+"F7.opExtrude","CAP_EDGE",EDGE,{"disambiguationData":[OSD([sQuery(id+"F6.wireOp",EDGE,"E5.sketch_text.stroke-80")])],"isStart":false});
            var Q194;
            Q194=makeQuery(id+"F7.opExtrude","CAP_EDGE",EDGE,{"disambiguationData":[OSD([sQuery(id+"F6.wireOp",EDGE,"E5.sketch_text.stroke-10")])],"isStart":false});
            var Q195;
            Q195=makeQuery(id+"F7.opExtrude","CAP_EDGE",EDGE,{"disambiguationData":[OSD([sQuery(id+"F6.wireOp",EDGE,"E5.sketch_text.stroke-12")])],"isStart":false});
            var Q196;
            Q196=makeQuery(id+"F7.opExtrude","CAP_EDGE",EDGE,{"disambiguationData":[OSD([sQuery(id+"F6.wireOp",EDGE,"E5.sketch_text.stroke-20")])],"isStart":false});
            var Q197;
            Q197=makeQuery(id+"F7.opExtrude","CAP_EDGE",EDGE,{"disambiguationData":[OSD([sQuery(id+"F6.wireOp",EDGE,"E5.sketch_text.stroke-8")])],"isStart":false});
            var Q198;
            Q198=makeQuery(id+"F7.opExtrude","CAP_EDGE",EDGE,{"disambiguationData":[OSD([sQuery(id+"F6.wireOp",EDGE,"E5.sketch_text.stroke-71")])],"isStart":false});
            var Q199;
            Q199=makeQuery(id+"F7.opExtrude","CAP_EDGE",EDGE,{"disambiguationData":[OSD([sQuery(id+"F6.wireOp",EDGE,"E5.sketch_text.stroke-63")])],"isStart":false});
            var Q200;
            Q200=makeQuery(id+"F7.opExtrude","CAP_EDGE",EDGE,{"disambiguationData":[OSD([sQuery(id+"F6.wireOp",EDGE,"E5.sketch_text.stroke-61")])],"isStart":false});
            var Q201;
            Q201=makeQuery(id+"F7.opExtrude","CAP_EDGE",EDGE,{"disambiguationData":[OSD([sQuery(id+"F6.wireOp",EDGE,"E5.sketch_text.stroke-73")])],"isStart":false});
            var Q202;
            Q202=makeQuery(id+"F7.opExtrude","CAP_EDGE",EDGE,{"disambiguationData":[OSD([sQuery(id+"F6.wireOp",EDGE,"E5.sketch_text.stroke-65")])],"isStart":false});
            var Q203;
            Q203=makeQuery(id+"F7.opExtrude","CAP_EDGE",EDGE,{"disambiguationData":[OSD([sQuery(id+"F6.wireOp",EDGE,"E5.sketch_text.stroke-137")])],"isStart":false});
            var Q204;
            Q204=makeQuery(id+"F7.opExtrude","CAP_EDGE",EDGE,{"disambiguationData":[OSD([sQuery(id+"F6.wireOp",EDGE,"E5.sketch_text.stroke-130")])],"isStart":false});
            var Q205;
            Q205=makeQuery(id+"F7.opExtrude","CAP_EDGE",EDGE,{"disambiguationData":[OSD([sQuery(id+"F6.wireOp",EDGE,"E5.sketch_text.stroke-138")])],"isStart":false});
            var Q206;
            Q206=makeQuery(id+"F7.opExtrude","CAP_EDGE",EDGE,{"disambiguationData":[OSD([sQuery(id+"F6.wireOp",EDGE,"E5.sketch_text.stroke-148")])],"isStart":false});
            var Q207;
            Q207=makeQuery(id+"F7.opExtrude","CAP_EDGE",EDGE,{"disambiguationData":[OSD([sQuery(id+"F6.wireOp",EDGE,"E5.sketch_text.stroke-141")])],"isStart":false});
            var Q208;
            Q208=makeQuery(id+"F7.opExtrude","CAP_EDGE",EDGE,{"disambiguationData":[OSD([sQuery(id+"F6.wireOp",EDGE,"E5.sketch_text.stroke-142")])],"isStart":false});
            var Q209;
            Q209=makeQuery(id+"F7.opExtrude","CAP_EDGE",EDGE,{"disambiguationData":[OSD([sQuery(id+"F6.wireOp",EDGE,"E5.sketch_text.stroke-150")])],"isStart":false});
            var Q210;
            Q210=makeQuery(id+"F7.opExtrude","CAP_EDGE",EDGE,{"disambiguationData":[OSD([sQuery(id+"F6.wireOp",EDGE,"E5.sketch_text.stroke-161")])],"isStart":false});
            var Q211;
            Q211=makeQuery(id+"F7.opExtrude","CAP_EDGE",EDGE,{"disambiguationData":[OSD([sQuery(id+"F6.wireOp",EDGE,"E5.sketch_text.stroke-170")])],"isStart":false});
            var Q212;
            Q212=makeQuery(id+"F7.opExtrude","CAP_EDGE",EDGE,{"disambiguationData":[OSD([sQuery(id+"F6.wireOp",EDGE,"E5.sketch_text.stroke-171")])],"isStart":false});
            var Q213;
            Q213=makeQuery(id+"F7.opExtrude","CAP_EDGE",EDGE,{"disambiguationData":[OSD([sQuery(id+"F6.wireOp",EDGE,"E5.sketch_text.stroke-173")])],"isStart":false});
            var Q214;
            Q214=makeQuery(id+"F7.opExtrude","CAP_EDGE",EDGE,{"disambiguationData":[OSD([sQuery(id+"F6.wireOp",EDGE,"E5.sketch_text.stroke-182")])],"isStart":false});
            var Q215;
            Q215=makeQuery(id+"F7.opExtrude","CAP_EDGE",EDGE,{"disambiguationData":[OSD([sQuery(id+"F6.wireOp",EDGE,"E5.sketch_text.stroke-167")])],"isStart":false});
            var Q216;
            Q216=makeQuery(id+"F7.opExtrude","CAP_EDGE",EDGE,{"disambiguationData":[OSD([sQuery(id+"F6.wireOp",EDGE,"E5.sketch_text.stroke-175")])],"isStart":false});
            var Q217;
            Q217=makeQuery(id+"F7.opExtrude","CAP_EDGE",EDGE,{"disambiguationData":[OSD([sQuery(id+"F6.wireOp",EDGE,"E5.sketch_text.stroke-168")])],"isStart":false});
            var Q218;
            Q218=makeQuery(id+"F7.opExtrude","CAP_EDGE",EDGE,{"disambiguationData":[OSD([sQuery(id+"F6.wireOp",EDGE,"E5.sketch_text.stroke-176")])],"isStart":false});
            var Q219;
            Q219=makeQuery(id+"F7.opExtrude","CAP_EDGE",EDGE,{"disambiguationData":[OSD([sQuery(id+"F6.wireOp",EDGE,"E5.sketch_text.stroke-209")])],"isStart":false});
            var Q220;
            Q220=makeQuery(id+"F7.opExtrude","CAP_EDGE",EDGE,{"disambiguationData":[OSD([sQuery(id+"F6.wireOp",EDGE,"E5.sketch_text.stroke-197")])],"isStart":false});
            var Q221;
            Q221=makeQuery(id+"F7.opExtrude","CAP_EDGE",EDGE,{"disambiguationData":[OSD([sQuery(id+"F6.wireOp",EDGE,"E5.sketch_text.stroke-205")])],"isStart":false});
            var Q222;
            Q222=makeQuery(id+"F7.opExtrude","CAP_EDGE",EDGE,{"disambiguationData":[OSD([sQuery(id+"F6.wireOp",EDGE,"E5.sketch_text.stroke-198")])],"isStart":false});
            var Q223;
            Q223=makeQuery(id+"F7.opExtrude","CAP_EDGE",EDGE,{"disambiguationData":[OSD([sQuery(id+"F6.wireOp",EDGE,"E5.sketch_text.stroke-206")])],"isStart":false});
            var Q224;
            Q224=makeQuery(id+"F7.opExtrude","CAP_EDGE",EDGE,{"disambiguationData":[OSD([sQuery(id+"F6.wireOp",EDGE,"E5.sketch_text.stroke-200")])],"isStart":false});
            var Q225;
            Q225=makeQuery(id+"F7.opExtrude","CAP_EDGE",EDGE,{"disambiguationData":[OSD([sQuery(id+"F6.wireOp",EDGE,"E5.sketch_text.stroke-225")])],"isStart":false});
            var Q226;
            Q226=makeQuery(id+"F7.opExtrude","CAP_EDGE",EDGE,{"disambiguationData":[OSD([sQuery(id+"F6.wireOp",EDGE,"E5.sketch_text.stroke-226")])],"isStart":false});
            var Q227;
            Q227=makeQuery(id+"F7.opExtrude","CAP_EDGE",EDGE,{"disambiguationData":[OSD([sQuery(id+"F6.wireOp",EDGE,"E5.sketch_text.stroke-220")])],"isStart":false});
            var Q228;
            Q228=makeQuery(id+"F7.opExtrude","CAP_EDGE",EDGE,{"disambiguationData":[OSD([sQuery(id+"F6.wireOp",EDGE,"E5.sketch_text.stroke-242")])],"isStart":false});
            var Q229;
            Q229=makeQuery(id+"F7.opExtrude","CAP_EDGE",EDGE,{"disambiguationData":[OSD([sQuery(id+"F6.wireOp",EDGE,"E5.sketch_text.stroke-243")])],"isStart":false});
            var Q230;
            Q230=makeQuery(id+"F7.opExtrude","CAP_EDGE",EDGE,{"disambiguationData":[OSD([sQuery(id+"F6.wireOp",EDGE,"E5.sketch_text.stroke-236")])],"isStart":false});
            var Q231;
            Q231=makeQuery(id+"F7.opExtrude","CAP_EDGE",EDGE,{"disambiguationData":[OSD([sQuery(id+"F6.wireOp",EDGE,"E5.sketch_text.stroke-237")])],"isStart":false});
            var Q232;
            Q232=makeQuery(id+"F7.opExtrude","CAP_EDGE",EDGE,{"disambiguationData":[OSD([sQuery(id+"F6.wireOp",EDGE,"E5.sketch_text.stroke-245")])],"isStart":false});
            var Q233;
            Q233=makeQuery(id+"F7.opExtrude","CAP_EDGE",EDGE,{"disambiguationData":[OSD([sQuery(id+"F6.wireOp",EDGE,"E5.sketch_text.stroke-249")])],"isStart":false});
            var Q234;
            Q234=makeQuery(id+"F7.opExtrude","CAP_EDGE",EDGE,{"disambiguationData":[OSD([sQuery(id+"F6.wireOp",EDGE,"E5.sketch_text.stroke-248")])],"isStart":false});
            var Q235;
            Q235=makeQuery(id+"F7.opExtrude","CAP_EDGE",EDGE,{"disambiguationData":[OSD([sQuery(id+"F6.wireOp",EDGE,"E5.sketch_text.stroke-258")])],"isStart":false});
            var Q236;
            Q236=makeQuery(id+"F7.opExtrude","CAP_EDGE",EDGE,{"disambiguationData":[OSD([sQuery(id+"F6.wireOp",EDGE,"E5.sketch_text.stroke-259")])],"isStart":false});
            var Q237;
            Q237=makeQuery(id+"F7.opExtrude","CAP_EDGE",EDGE,{"disambiguationData":[OSD([sQuery(id+"F6.wireOp",EDGE,"E5.sketch_text.stroke-260")])],"isStart":false});
            var Q238;
            Q238=makeQuery(id+"F7.opExtrude","CAP_EDGE",EDGE,{"disambiguationData":[OSD([sQuery(id+"F6.wireOp",EDGE,"E5.sketch_text.stroke-261")])],"isStart":false});
            var Q239;
            Q239=makeQuery(id+"F7.opExtrude","CAP_EDGE",EDGE,{"disambiguationData":[OSD([sQuery(id+"F6.wireOp",EDGE,"E5.sketch_text.stroke-262")])],"isStart":false});
            var Q240;
            Q240=makeQuery(id+"F7.opExtrude","CAP_EDGE",EDGE,{"disambiguationData":[OSD([sQuery(id+"F6.wireOp",EDGE,"E5.sketch_text.stroke-273")])],"isStart":false});
            var Q241;
            Q241=makeQuery(id+"F7.opExtrude","CAP_EDGE",EDGE,{"disambiguationData":[OSD([sQuery(id+"F6.wireOp",EDGE,"E5.sketch_text.stroke-274")])],"isStart":false});
            var Q242;
            Q242=makeQuery(id+"F7.opExtrude","CAP_EDGE",EDGE,{"disambiguationData":[OSD([sQuery(id+"F6.wireOp",EDGE,"E5.sketch_text.stroke-275")])],"isStart":false});
            var Q243;
            Q243=makeQuery(id+"F7.opExtrude","CAP_EDGE",EDGE,{"disambiguationData":[OSD([sQuery(id+"F6.wireOp",EDGE,"E5.sketch_text.stroke-283")])],"isStart":false});
            var Q244;
            Q244=makeQuery(id+"F7.opExtrude","CAP_EDGE",EDGE,{"disambiguationData":[OSD([sQuery(id+"F6.wireOp",EDGE,"E5.sketch_text.stroke-276")])],"isStart":false});
            var Q245;
            Q245=makeQuery(id+"F7.opExtrude","CAP_EDGE",EDGE,{"disambiguationData":[OSD([sQuery(id+"F6.wireOp",EDGE,"E5.sketch_text.stroke-284")])],"isStart":false});
            var Q246;
            Q246=makeQuery(id+"F7.opExtrude","CAP_EDGE",EDGE,{"disambiguationData":[OSD([sQuery(id+"F6.wireOp",EDGE,"E5.sketch_text.stroke-289")])],"isStart":false});
            var Q247;
            Q247=makeQuery(id+"F7.opExtrude","CAP_EDGE",EDGE,{"disambiguationData":[OSD([sQuery(id+"F6.wireOp",EDGE,"E5.sketch_text.stroke-297")])],"isStart":false});
            var Q248;
            Q248=makeQuery(id+"F7.opExtrude","CAP_EDGE",EDGE,{"disambiguationData":[OSD([sQuery(id+"F6.wireOp",EDGE,"E5.sketch_text.stroke-305")])],"isStart":false});
            var Q249;
            Q249=makeQuery(id+"F7.opExtrude","CAP_EDGE",EDGE,{"disambiguationData":[OSD([sQuery(id+"F6.wireOp",EDGE,"E5.sketch_text.stroke-299")])],"isStart":false});
            var Q250;
            Q250=makeQuery(id+"F7.opExtrude","CAP_EDGE",EDGE,{"disambiguationData":[OSD([sQuery(id+"F6.wireOp",EDGE,"E5.sketch_text.stroke-302")])],"isStart":false});
            var Q251;
            Q251=makeQuery(id+"F7.opExtrude","CAP_EDGE",EDGE,{"disambiguationData":[OSD([sQuery(id+"F6.wireOp",EDGE,"E5.sketch_text.stroke-310")])],"isStart":false});
            var Q252;
            Q252=makeQuery(id+"F7.opExtrude","CAP_EDGE",EDGE,{"disambiguationData":[OSD([sQuery(id+"F6.wireOp",EDGE,"E5.sketch_text.stroke-303")])],"isStart":false});
            var Q253;
            Q253=makeQuery(id+"F7.opExtrude","CAP_EDGE",EDGE,{"disambiguationData":[OSD([sQuery(id+"F6.wireOp",EDGE,"E5.sketch_text.stroke-40")])],"isStart":false});
            var Q254;
            Q254=makeQuery(id+"F7.opExtrude","CAP_EDGE",EDGE,{"disambiguationData":[OSD([sQuery(id+"F6.wireOp",EDGE,"E5.sketch_text.stroke-42")])],"isStart":false});
            var Q255;
            Q255=makeQuery(id+"F7.opExtrude","CAP_EDGE",EDGE,{"disambiguationData":[OSD([sQuery(id+"F6.wireOp",EDGE,"E5.sketch_text.stroke-114")])],"isStart":false});
            var Q256;
            Q256=makeQuery(id+"F7.opExtrude","CAP_EDGE",EDGE,{"disambiguationData":[OSD([sQuery(id+"F6.wireOp",EDGE,"E5.sketch_text.stroke-90")])],"isStart":false});
            var Q257;
            Q257=makeQuery(id+"F7.opExtrude","CAP_EDGE",EDGE,{"disambiguationData":[OSD([sQuery(id+"F6.wireOp",EDGE,"E5.sketch_text.stroke-106")])],"isStart":false});
            var Q258;
            Q258=makeQuery(id+"F7.opExtrude","CAP_EDGE",EDGE,{"disambiguationData":[OSD([sQuery(id+"F6.wireOp",EDGE,"E5.sketch_text.stroke-102")])],"isStart":false});
            var Q259;
            Q259=makeQuery(id+"F7.opExtrude","CAP_EDGE",EDGE,{"disambiguationData":[OSD([sQuery(id+"F6.wireOp",EDGE,"E5.sketch_text.stroke-17")])],"isStart":false});
            var Q260;
            Q260=makeQuery(id+"F7.opExtrude","CAP_EDGE",EDGE,{"disambiguationData":[OSD([sQuery(id+"F6.wireOp",EDGE,"E5.sketch_text.stroke-11")])],"isStart":false});
            var Q261;
            Q261=makeQuery(id+"F7.opExtrude","CAP_EDGE",EDGE,{"disambiguationData":[OSD([sQuery(id+"F6.wireOp",EDGE,"E5.sketch_text.stroke-13")])],"isStart":false});
            var Q262;
            Q262=makeQuery(id+"F7.opExtrude","CAP_EDGE",EDGE,{"disambiguationData":[OSD([sQuery(id+"F6.wireOp",EDGE,"E5.sketch_text.stroke-16")])],"isStart":false});
            var Q263;
            Q263=makeQuery(id+"F7.opExtrude","CAP_EDGE",EDGE,{"disambiguationData":[OSD([sQuery(id+"F6.wireOp",EDGE,"E5.sketch_text.stroke-72")])],"isStart":false});
            var Q264;
            Q264=makeQuery(id+"F7.opExtrude","CAP_EDGE",EDGE,{"disambiguationData":[OSD([sQuery(id+"F6.wireOp",EDGE,"E5.sketch_text.stroke-64")])],"isStart":false});
            var Q265;
            Q265=makeQuery(id+"F7.opExtrude","CAP_EDGE",EDGE,{"disambiguationData":[OSD([sQuery(id+"F6.wireOp",EDGE,"E5.sketch_text.stroke-62")])],"isStart":false});
            var Q266;
            Q266=makeQuery(id+"F7.opExtrude","CAP_EDGE",EDGE,{"disambiguationData":[OSD([sQuery(id+"F6.wireOp",EDGE,"E5.sketch_text.stroke-67")])],"isStart":false});
            var Q267;
            Q267=makeQuery(id+"F7.opExtrude","CAP_EDGE",EDGE,{"disambiguationData":[OSD([sQuery(id+"F6.wireOp",EDGE,"E5.sketch_text.stroke-122")])],"isStart":false});
            var Q268;
            Q268=makeQuery(id+"F7.opExtrude","CAP_EDGE",EDGE,{"disambiguationData":[OSD([sQuery(id+"F6.wireOp",EDGE,"E5.sketch_text.stroke-123")])],"isStart":false});
            var Q269;
            Q269=makeQuery(id+"F7.opExtrude","CAP_EDGE",EDGE,{"disambiguationData":[OSD([sQuery(id+"F6.wireOp",EDGE,"E5.sketch_text.stroke-131")])],"isStart":false});
            var Q270;
            Q270=makeQuery(id+"F7.opExtrude","CAP_EDGE",EDGE,{"disambiguationData":[OSD([sQuery(id+"F6.wireOp",EDGE,"E5.sketch_text.stroke-155")])],"isStart":false});
            var Q271;
            Q271=makeQuery(id+"F7.opExtrude","CAP_EDGE",EDGE,{"disambiguationData":[OSD([sQuery(id+"F6.wireOp",EDGE,"E5.sketch_text.stroke-156")])],"isStart":false});
            var Q272;
            Q272=makeQuery(id+"F7.opExtrude","CAP_EDGE",EDGE,{"disambiguationData":[OSD([sQuery(id+"F6.wireOp",EDGE,"E5.sketch_text.stroke-149")])],"isStart":false});
            var Q273;
            Q273=makeQuery(id+"F7.opExtrude","CAP_EDGE",EDGE,{"disambiguationData":[OSD([sQuery(id+"F6.wireOp",EDGE,"E5.sketch_text.stroke-157")])],"isStart":false});
            var Q274;
            Q274=makeQuery(id+"F7.opExtrude","CAP_EDGE",EDGE,{"disambiguationData":[OSD([sQuery(id+"F6.wireOp",EDGE,"E5.sketch_text.stroke-136")])],"isStart":false});
            var Q275;
            Q275=makeQuery(id+"F7.opExtrude","CAP_EDGE",EDGE,{"disambiguationData":[OSD([sQuery(id+"F6.wireOp",EDGE,"E5.sketch_text.stroke-174")])],"isStart":false});
            var Q276;
            Q276=makeQuery(id+"F7.opExtrude","CAP_EDGE",EDGE,{"disambiguationData":[OSD([sQuery(id+"F6.wireOp",EDGE,"E5.sketch_text.stroke-194")])],"isStart":false});
            var Q277;
            Q277=makeQuery(id+"F7.opExtrude","CAP_EDGE",EDGE,{"disambiguationData":[OSD([sQuery(id+"F6.wireOp",EDGE,"E5.sketch_text.stroke-210")])],"isStart":false});
            var Q278;
            Q278=makeQuery(id+"F7.opExtrude","CAP_EDGE",EDGE,{"disambiguationData":[OSD([sQuery(id+"F6.wireOp",EDGE,"E5.sketch_text.stroke-204")])],"isStart":false});
            var Q279;
            Q279=makeQuery(id+"F7.opExtrude","CAP_EDGE",EDGE,{"disambiguationData":[OSD([sQuery(id+"F6.wireOp",EDGE,"E5.sketch_text.stroke-199")])],"isStart":false});
            var Q280;
            Q280=makeQuery(id+"F7.opExtrude","CAP_EDGE",EDGE,{"disambiguationData":[OSD([sQuery(id+"F6.wireOp",EDGE,"E5.sketch_text.stroke-221")])],"isStart":false});
            var Q281;
            Q281=makeQuery(id+"F7.opExtrude","CAP_EDGE",EDGE,{"disambiguationData":[OSD([sQuery(id+"F6.wireOp",EDGE,"E5.sketch_text.stroke-222")])],"isStart":false});
            var Q282;
            Q282=makeQuery(id+"F7.opExtrude","CAP_EDGE",EDGE,{"disambiguationData":[OSD([sQuery(id+"F6.wireOp",EDGE,"E5.sketch_text.stroke-223")])],"isStart":false});
            var Q283;
            Q283=makeQuery(id+"F7.opExtrude","CAP_EDGE",EDGE,{"disambiguationData":[OSD([sQuery(id+"F6.wireOp",EDGE,"E5.sketch_text.stroke-224")])],"isStart":false});
            var Q284;
            Q284=makeQuery(id+"F7.opExtrude","CAP_EDGE",EDGE,{"disambiguationData":[OSD([sQuery(id+"F6.wireOp",EDGE,"E5.sketch_text.stroke-241")])],"isStart":false});
            var Q285;
            Q285=makeQuery(id+"F7.opExtrude","CAP_EDGE",EDGE,{"disambiguationData":[OSD([sQuery(id+"F6.wireOp",EDGE,"E5.sketch_text.stroke-244")])],"isStart":false});
            var Q286;
            Q286=makeQuery(id+"F7.opExtrude","CAP_EDGE",EDGE,{"disambiguationData":[OSD([sQuery(id+"F6.wireOp",EDGE,"E5.sketch_text.stroke-238")])],"isStart":false});
            var Q287;
            Q287=makeQuery(id+"F7.opExtrude","CAP_EDGE",EDGE,{"disambiguationData":[OSD([sQuery(id+"F6.wireOp",EDGE,"E5.sketch_text.stroke-298")])],"isStart":false});
            var Q288;
            Q288=makeQuery(id+"F7.opExtrude","CAP_EDGE",EDGE,{"disambiguationData":[OSD([sQuery(id+"F6.wireOp",EDGE,"E5.sketch_text.stroke-47")])],"isStart":false});
            var Q289;
            Q289=makeQuery(id+"F7.opExtrude","CAP_EDGE",EDGE,{"disambiguationData":[OSD([sQuery(id+"F6.wireOp",EDGE,"E5.sketch_text.stroke-103")])],"isStart":false});
            var Q290;
            Q290=makeQuery(id+"F7.opExtrude","CAP_EDGE",EDGE,{"disambiguationData":[OSD([sQuery(id+"F6.wireOp",EDGE,"E5.sketch_text.stroke-21")])],"isStart":false});
            var Q291;
            Q291=makeQuery(id+"F7.opExtrude","CAP_EDGE",EDGE,{"disambiguationData":[OSD([sQuery(id+"F6.wireOp",EDGE,"E5.sketch_text.stroke-15")])],"isStart":false});
            var Q292;
            Q292=makeQuery(id+"F7.opExtrude","CAP_EDGE",EDGE,{"disambiguationData":[OSD([sQuery(id+"F6.wireOp",EDGE,"E5.sketch_text.stroke-69")])],"isStart":false});
            var Q293;
            Q293=makeQuery(id+"F7.opExtrude","CAP_EDGE",EDGE,{"disambiguationData":[OSD([sQuery(id+"F6.wireOp",EDGE,"E5.sketch_text.stroke-66")])],"isStart":false});
            var Q294;
            Q294=makeQuery(id+"F7.opExtrude","CAP_EDGE",EDGE,{"disambiguationData":[OSD([sQuery(id+"F6.wireOp",EDGE,"E5.sketch_text.stroke-121")])],"isStart":false});
            var Q295;
            Q295=makeQuery(id+"F7.opExtrude","CAP_EDGE",EDGE,{"disambiguationData":[OSD([sQuery(id+"F6.wireOp",EDGE,"E5.sketch_text.stroke-119")])],"isStart":false});
            var Q296;
            Q296=makeQuery(id+"F7.opExtrude","CAP_EDGE",EDGE,{"disambiguationData":[OSD([sQuery(id+"F6.wireOp",EDGE,"E5.sketch_text.stroke-120")])],"isStart":false});
            var Q297;
            Q297=makeQuery(id+"F7.opExtrude","CAP_EDGE",EDGE,{"disambiguationData":[OSD([sQuery(id+"F6.wireOp",EDGE,"E5.sketch_text.stroke-153")])],"isStart":false});
            var Q298;
            Q298=makeQuery(id+"F7.opExtrude","CAP_EDGE",EDGE,{"disambiguationData":[OSD([sQuery(id+"F6.wireOp",EDGE,"E5.sketch_text.stroke-154")])],"isStart":false});
            var Q299;
            Q299=makeQuery(id+"F7.opExtrude","CAP_EDGE",EDGE,{"disambiguationData":[OSD([sQuery(id+"F6.wireOp",EDGE,"E5.sketch_text.stroke-132")])],"isStart":false});
            var Q300;
            Q300=makeQuery(id+"F7.opExtrude","CAP_EDGE",EDGE,{"disambiguationData":[OSD([sQuery(id+"F6.wireOp",EDGE,"E5.sketch_text.stroke-133")])],"isStart":false});
            var Q301;
            Q301=makeQuery(id+"F7.opExtrude","CAP_EDGE",EDGE,{"disambiguationData":[OSD([sQuery(id+"F6.wireOp",EDGE,"E5.sketch_text.stroke-134")])],"isStart":false});
            var Q302;
            Q302=makeQuery(id+"F7.opExtrude","CAP_EDGE",EDGE,{"disambiguationData":[OSD([sQuery(id+"F6.wireOp",EDGE,"E5.sketch_text.stroke-135")])],"isStart":false});
            var Q303;
            Q303=makeQuery(id+"F7.opExtrude","CAP_EDGE",EDGE,{"disambiguationData":[OSD([sQuery(id+"F6.wireOp",EDGE,"E5.sketch_text.stroke-151")])],"isStart":false});
            var Q304;
            Q304=makeQuery(id+"F7.opExtrude","CAP_EDGE",EDGE,{"disambiguationData":[OSD([sQuery(id+"F6.wireOp",EDGE,"E5.sketch_text.stroke-195")])],"isStart":false});
            var Q305;
            Q305=makeQuery(id+"F7.opExtrude","CAP_EDGE",EDGE,{"disambiguationData":[OSD([sQuery(id+"F6.wireOp",EDGE,"E5.sketch_text.stroke-239")])],"isStart":false});
            var Q306;
            Q306=makeQuery(id+"F7.opExtrude","CAP_EDGE",EDGE,{"disambiguationData":[OSD([sQuery(id+"F6.wireOp",EDGE,"E5.sketch_text.stroke-240")])],"isStart":false});
            var Q307;
            Q307=makeQuery(id+"F7.opExtrude","CAP_EDGE",EDGE,{"disambiguationData":[OSD([sQuery(id+"F6.wireOp",EDGE,"E5.sketch_text.stroke-41")])],"isStart":false});
            var Q308;
            Q308=makeQuery(id+"F7.opExtrude","CAP_EDGE",EDGE,{"disambiguationData":[OSD([sQuery(id+"F6.wireOp",EDGE,"E5.sketch_text.stroke-91")])],"isStart":false});
            var Q309;
            Q309=makeQuery(id+"F7.opExtrude","CAP_EDGE",EDGE,{"disambiguationData":[OSD([sQuery(id+"F6.wireOp",EDGE,"E5.sketch_text.stroke-14")])],"isStart":false});
            var Q310;
            Q310=makeQuery(id+"F7.opExtrude","CAP_EDGE",EDGE,{"disambiguationData":[OSD([sQuery(id+"F6.wireOp",EDGE,"E5.sketch_text.stroke-68")])],"isStart":false});
            var Q311;
            Q311=makeQuery(id+"F7.opExtrude","CAP_EDGE",EDGE,{"disambiguationData":[OSD([sQuery(id+"F6.wireOp",EDGE,"E5.sketch_text.stroke-152")])],"isStart":false});
            var Q312;
            Q312=makeQuery(id+"F7.opExtrude","CAP_EDGE",EDGE,{"disambiguationData":[OSD([sQuery(id+"F6.wireOp",EDGE,"E5.sketch_text.stroke-196")])],"isStart":false});
            var Q313;
            Q313=makeQuery(id+"F7.opExtrude","CAP_EDGE",EDGE,{"disambiguationData":[OSD([sQuery(id+"F6.wireOp",EDGE,"E5.sketch_text.stroke-92")])],"isStart":false});
            var Q314;
            Q314=makeQuery(id+"F7.opExtrude","CAP_EDGE",EDGE,{"disambiguationData":[OSD([sQuery(id+"F6.wireOp",EDGE,"E5.sketch_text.stroke-93")])],"isStart":false});
            fillet(context, id + "F8", {"entities" : qUnion([Q0, Q1, Q2, Q3, Q4, Q5, Q6, Q7, Q8, Q9, Q10, Q11, Q12, Q13, Q14, Q15, Q16, Q17, Q18, Q19, Q20, Q21, Q22, Q23, Q24, Q25, Q26, Q27, Q28, Q29, Q30, Q31, Q32, Q33, Q34, Q35, Q36, Q37, Q38, Q39, Q40, Q41, Q42, Q43, Q44, Q45, Q46, Q47, Q48, Q49, Q50, Q51, Q52, Q53, Q54, Q55, Q56, Q57, Q58, Q59, Q60, Q61, Q62, Q63, Q64, Q65, Q66, Q67, Q68, Q69, Q70, Q71, Q72, Q73, Q74, Q75, Q76, Q77, Q78, Q79, Q80, Q81, Q82, Q83, Q84, Q85, Q86, Q87, Q88, Q89, Q90, Q91, Q92, Q93, Q94, Q95, Q96, Q97, Q98, Q99, Q100, Q101, Q102, Q103, Q104, Q105, Q106, Q107, Q108, Q109, Q110, Q111, Q112, Q113, Q114, Q115, Q116, Q117, Q118, Q119, Q120, Q121, Q122, Q123, Q124, Q125, Q126, Q127, Q128, Q129, Q130, Q131, Q132, Q133, Q134, Q135, Q136, Q137, Q138, Q139, Q140, Q141, Q142, Q143, Q144, Q145, Q146, Q147, Q148, Q149, Q150, Q151, Q152, Q153, Q154, Q155, Q156, Q157, Q158, Q159, Q160, Q161, Q162, Q163, Q164, Q165, Q166, Q167, Q168, Q169, Q170, Q171, Q172, Q173, Q174, Q175, Q176, Q177, Q178, Q179, Q180, Q181, Q182, Q183, Q184, Q185, Q186, Q187, Q188, Q189, Q190, Q191, Q192, Q193, Q194, Q195, Q196, Q197, Q198, Q199, Q200, Q201, Q202, Q203, Q204, Q205, Q206, Q207, Q208, Q209, Q210, Q211, Q212, Q213, Q214, Q215, Q216, Q217, Q218, Q219, Q220, Q221, Q222, Q223, Q224, Q225, Q226, Q227, Q228, Q229, Q230, Q231, Q232, Q233, Q234, Q235, Q236, Q237, Q238, Q239, Q240, Q241, Q242, Q243, Q244, Q245, Q246, Q247, Q248, Q249, Q250, Q251, Q252, Q253, Q254, Q255, Q256, Q257, Q258, Q259, Q260, Q261, Q262, Q263, Q264, Q265, Q266, Q267, Q268, Q269, Q270, Q271, Q272, Q273, Q274, Q275, Q276, Q277, Q278, Q279, Q280, Q281, Q282, Q283, Q284, Q285, Q286, Q287, Q288, Q289, Q290, Q291, Q292, Q293, Q294, Q295, Q296, Q297, Q298, Q299, Q300, Q301, Q302, Q303, Q304, Q305, Q306, Q307, Q308, Q309, Q310, Q311, Q312, Q313, Q314]), "radius" : 0.08 * mm, "tangentPropagation" : true, "allowEdgeOverflow" : false});
        }
    });
